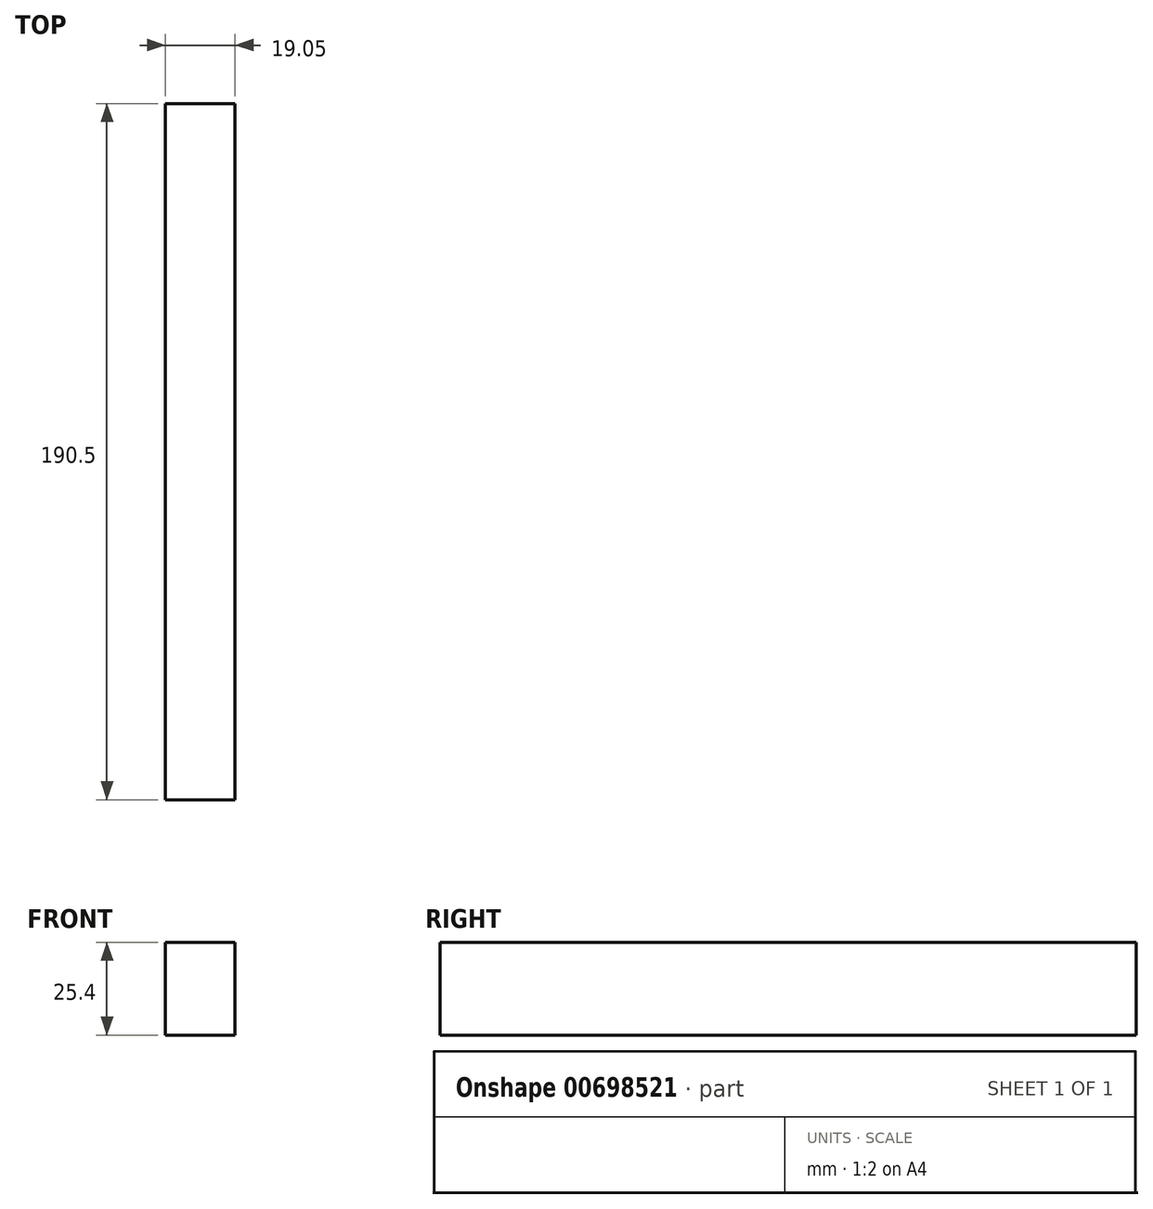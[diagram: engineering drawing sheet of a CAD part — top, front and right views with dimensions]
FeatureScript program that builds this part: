
annotation { "Feature Type Name" : "Feature", "Feature Type Description" : "" }
export const myFeature = defineFeature(function(context is Context, id is Id, definition is map)
    precondition{}
    {
        {
            var Q0;
            Q0=qCreatedBy(makeId("Right.planeOp"),FACE);
            var sketch = newSketch(context, id + "F0", { "sketchPlane" : qUnion([Q0])});
            skLineSegment(sketch, "E0.bottom", {"start": v(-113.7, -62.18) * mm, "end": v(76.8, -62.18) * mm});
            skLineSegment(sketch, "E0.top", {"start": v(-113.7, -36.78) * mm, "end": v(76.8, -36.78) * mm});
            skLineSegment(sketch, "E0.left", {"start": v(-113.7, -62.18) * mm, "end": v(-113.7, -36.78) * mm});
            skLineSegment(sketch, "E0.right", {"start": v(76.8, -62.18) * mm, "end": v(76.8, -36.78) * mm});
            skSolve(sketch);
        }
        {
            var Q0;
            Q0 = qSketchRegion(id + "F0", true);
            extrude(context, id + "F1", {"entities" : qUnion([Q0]), "depth" : 19.05 * mm, "offsetDistance" : 25.4 * mm});
        }
    });
